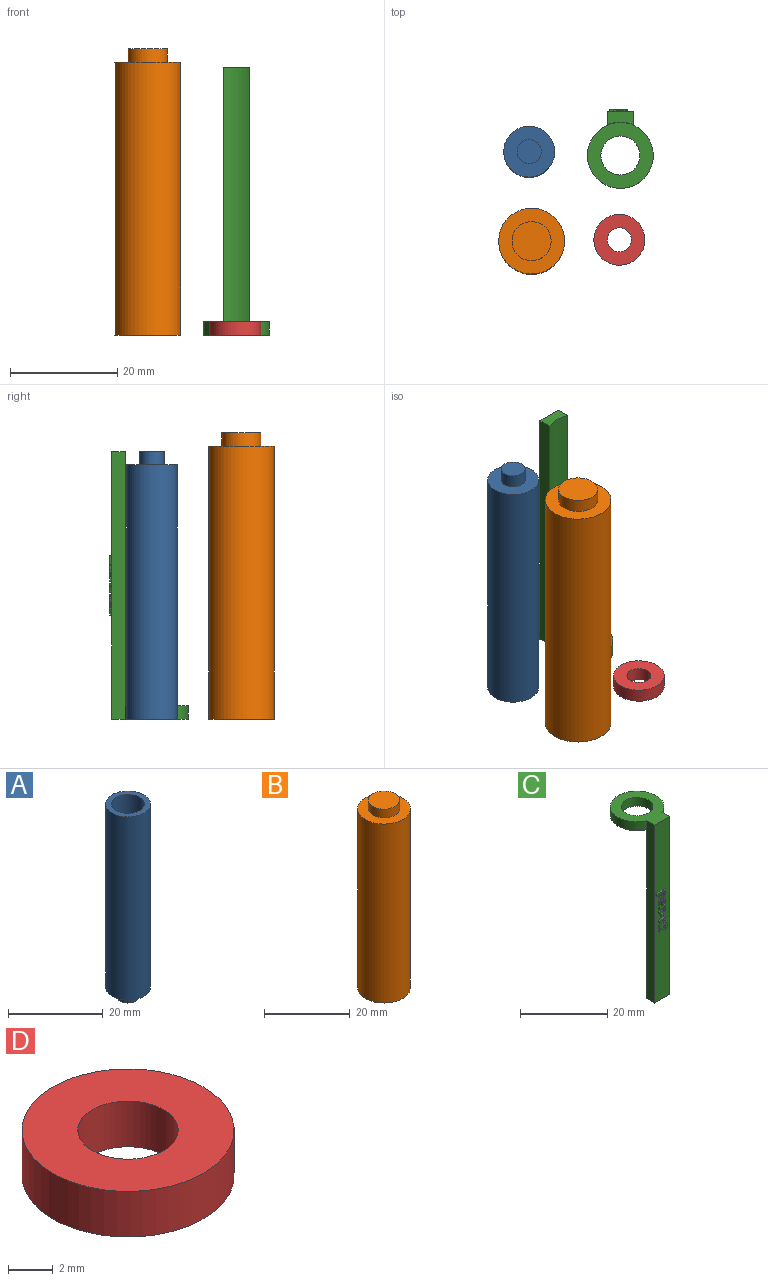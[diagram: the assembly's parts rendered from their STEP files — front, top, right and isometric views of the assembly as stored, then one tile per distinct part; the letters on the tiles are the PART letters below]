
ASSEMBLY  parts=4 mates=3
PART A: 7 faces, bbox 9.5x9.5x50 mm
  f0: cylinder r=3.5mm len=45mm, axis (0,0,-1), area 989.6mm2, adj f2,f3
  f1: cylinder r=4.75mm len=47.5mm, axis (0,0,-1), area 1417.6mm2, adj f2,f4
  f2: plane 9.5x9.5mm, normal (0,0,1), area 32.4mm2, adj f0,f1
  f3: plane 7x7mm, normal (0,0,1), area 38.5mm2, adj f0
  f4: plane 9.5x9.5mm, normal (0,0,-1), area 55mm2, adj f1,f5
  f5: cylinder r=2.25mm len=4.5mm, axis (0,0,1), area 35.3mm2, adj f4,f6
  f6: plane 4.5x4.5mm, normal (0,0,-1), area 15.9mm2, adj f5
PART B: 7 faces, bbox 12.3x12.3x53.5 mm
  f0: cylinder r=4.9mm len=50mm, axis (0,0,-1), area 1539.4mm2, adj f2,f3
  f1: cylinder r=6.15mm len=51mm, axis (0,0,-1), area 1970.7mm2, adj f2,f4
  f2: plane 12.3x12.3mm, normal (0,0,-1), area 43.4mm2, adj f0,f1
  f3: plane 9.8x9.8mm, normal (0,0,-1), area 75.4mm2, adj f0
  f4: plane 12.3x12.3mm, normal (0,0,1), area 77mm2, adj f1,f5
  f5: cylinder r=3.65mm len=7.3mm, axis (0,0,-1), area 57.3mm2, adj f4,f6
  f6: plane 7.3x7.3mm, normal (0,0,1), area 41.9mm2, adj f5
PART C: 115 faces, bbox 12.3x14.7x50 mm
  f0: plane 50x4.89mm, normal (0,-1,0), area 231.9mm2, adj f2,f6,f7,f8,f16,f17,f18,f19
  f1: cylinder r=6.15mm len=12.3mm, axis (0,0,-1), area 84mm2, adj f2,f4,f6,f7
  f2: plane 14.29x12.3mm, normal (0,0,1), area 87.5mm2, adj f0,f1,f3,f6,f7
  f3: cylinder r=3.65mm len=7.3mm, axis (0,0,-1), area 57.3mm2, adj f2,f4
  f4: plane 12.3x12.3mm, normal (0,0,-1), area 77mm2, adj f1,f3,f5
  f5: cylinder r=6.15mm len=47.5mm, axis (0,0,1), area 238.7mm2, adj f4,f6,f7,f8
  f6: plane 50x2.5mm, normal (-1,0,0), area 125mm2, adj f0,f1,f2,f5,f8
  f7: plane 50x2.5mm, normal (1,0,0), area 125mm2, adj f0,f1,f2,f5,f8
  f8: plane 4.89x2.5mm, normal (0,0,-1), area 10.6mm2, adj f0,f5,f6,f7
  f9: extruded ~0.4x0.28mm, area 0.1mm2, adj f10,f31,f32,f33
  f10: extruded ~0.4x0.27mm, area 0.1mm2, adj f9,f11,f32,f33
  f11: extruded ~0.42x0.4mm, area 0.2mm2, adj f10,f12,f32,f33
  f12: extruded ~0.57x0.4mm, area 0.3mm2, adj f11,f13,f32,f33
  f13: extruded ~0.4x0.29mm, area 0.1mm2, adj f12,f14,f32,f33
  f14: extruded ~0.44x0.4mm, area 0.2mm2, adj f13,f15,f32,f33
  f15: plane 0.4x0.06mm, normal (0,0,-1), area 0mm2, adj f14,f31,f32,f33
  f16: extruded ~0.52x0.4mm, area 0.2mm2, adj f0,f17,f30,f32
  f17: extruded ~0.4x0.38mm, area 0.2mm2, adj f0,f16,f18,f32
  f18: extruded ~0.4x0.34mm, area 0.2mm2, adj f0,f17,f19,f32
  f19: extruded ~0.52x0.4mm, area 0.2mm2, adj f0,f18,f20,f32
  f20: extruded ~0.72x0.4mm, area 0.3mm2, adj f0,f19,f21,f32
  f21: extruded ~0.52x0.4mm, area 0.2mm2, adj f0,f20,f22,f32
  f22: extruded ~0.54x0.4mm, area 0.3mm2, adj f0,f21,f23,f32
  f23: plane 0.4x0.02mm, normal (1,0,0), area 0mm2, adj f0,f22,f24,f32
  f24: plane 0.4x0.24mm, normal (0.28,0,-0.96), area 0.1mm2, adj f0,f23,f25,f32
  f25: plane 0.42x0.4mm, normal (1,0,0), area 0.2mm2, adj f0,f24,f26,f32
  f26: plane 2.72x0.4mm, normal (0,0,1), area 1.1mm2, adj f0,f25,f27,f32
  f27: plane 0.51x0.4mm, normal (-1,0,0), area 0.2mm2, adj f0,f26,f28,f32
  f28: plane 0.76x0.4mm, normal (0,0,-1), area 0.3mm2, adj f0,f27,f29,f32
  f29: extruded ~0.4x0.27mm, area 0.1mm2, adj f0,f28,f30,f32
  f30: plane 0.4x0.03mm, normal (-1,0,0), area 0mm2, adj f0,f16,f29,f32
  f31: extruded ~0.4x0.39mm, area 0.2mm2, adj f9,f15,f32,f33
  f32: plane 2.75x1.76mm, normal (0,-1,0), area 2.8mm2, adj f9,f10,f11,f12,f13,f14,f15,f16
  f33: plane 1.13x0.72mm, normal (0,-1,0), area 0.7mm2, adj f9,f10,f11,f12,f13,f14,f15,f31
  f34: extruded ~0.71x0.4mm, area 0.3mm2, adj f0,f35,f53,f54
  f35: extruded ~0.4x0.37mm, area 0.2mm2, adj f0,f34,f36,f54
  f36: extruded ~0.4x0.29mm, area 0.1mm2, adj f0,f35,f37,f54
  f37: plane 0.4x0.4mm, normal (0,0,-1), area 0.2mm2, adj f0,f36,f38,f54
  f38: extruded ~0.4x0.32mm, area 0.1mm2, adj f0,f37,f39,f54
  f39: extruded ~0.4x0.32mm, area 0.1mm2, adj f0,f38,f40,f54
  f40: extruded ~0.4x0.34mm, area 0.1mm2, adj f0,f39,f41,f54
  f41: extruded ~0.4x0.34mm, area 0.1mm2, adj f0,f40,f42,f54
  f42: plane 1.22x0.4mm, normal (-1,0,0), area 0.5mm2, adj f0,f41,f43,f54
  f43: plane 0.4x0.25mm, normal (0,0,-1), area 0.1mm2, adj f0,f42,f44,f54
  f44: extruded ~0.63x0.4mm, area 0.3mm2, adj f0,f43,f45,f54
  f45: extruded ~0.62x0.4mm, area 0.3mm2, adj f0,f44,f46,f54
  f46: extruded ~0.66x0.4mm, area 0.3mm2, adj f0,f45,f47,f54
  f47: extruded ~0.73x0.4mm, area 0.3mm2, adj f0,f46,f53,f54
  f48: extruded ~0.4x0.26mm, area 0.1mm2, adj f49,f52,f54,f55
  f49: extruded ~0.4x0.26mm, area 0.1mm2, adj f48,f50,f54,f55
  f50: extruded ~0.4x0.29mm, area 0.1mm2, adj f49,f51,f54,f55
  f51: plane 0.72x0.4mm, normal (1,0,0), area 0.3mm2, adj f50,f52,f54,f55
  f52: extruded ~0.4x0.29mm, area 0.1mm2, adj f48,f51,f54,f55
  f53: extruded ~0.71x0.4mm, area 0.3mm2, adj f0,f34,f47,f54
  f54: plane 1.95x1.74mm, normal (0,-1,0), area 2.1mm2, adj f34,f35,f36,f37,f38,f39,f40,f41
  f55: plane 0.72x0.4mm, normal (0,-1,0), area 0.2mm2, adj f48,f49,f50,f51,f52
  f56: plane 0.51x0.4mm, normal (-1,0,0), area 0.2mm2, adj f0,f57,f72,f73
  f57: plane 1.23x0.4mm, normal (0,0,-1), area 0.5mm2, adj f0,f56,f58,f73
  f58: extruded ~0.51x0.4mm, area 0.2mm2, adj f0,f57,f59,f73
  f59: extruded ~0.5x0.4mm, area 0.2mm2, adj f0,f58,f60,f73
  f60: extruded ~0.4x0.34mm, area 0.1mm2, adj f0,f59,f61,f73
  f61: extruded ~0.4x0.24mm, area 0.1mm2, adj f0,f60,f62,f73
  f62: plane 0.4x0.03mm, normal (1,0,0), area 0mm2, adj f0,f61,f63,f73
  f63: plane 0.4x0.24mm, normal (0.28,0,-0.96), area 0.1mm2, adj f0,f62,f64,f73
  f64: plane 0.4x0.39mm, normal (1,0,0), area 0.2mm2, adj f0,f63,f65,f73
  f65: plane 1.89x0.4mm, normal (0,0,1), area 0.8mm2, adj f0,f64,f66,f73
  f66: plane 0.51x0.4mm, normal (-1,0,0), area 0.2mm2, adj f0,f65,f67,f73
  f67: plane 0.89x0.4mm, normal (0,0,-1), area 0.4mm2, adj f0,f66,f68,f73
  f68: extruded ~0.48x0.4mm, area 0.2mm2, adj f0,f67,f69,f73
  f69: extruded ~0.4x0.31mm, area 0.1mm2, adj f0,f68,f70,f73
  f70: extruded ~0.4x0.23mm, area 0.1mm2, adj f0,f69,f71,f73
  f71: extruded ~0.4x0.31mm, area 0.1mm2, adj f0,f70,f72,f73
  f72: plane 1.1x0.4mm, normal (0,0,1), area 0.4mm2, adj f0,f56,f71,f73
  f73: plane 1.92x1.74mm, normal (0,-1,0), area 2.2mm2, adj f56,f57,f58,f59,f60,f61,f62,f63
  f74: plane 0.42x0.4mm, normal (0,0,1), area 0.2mm2, adj f0,f75,f77,f78
  f75: plane 0.91x0.4mm, normal (-1,0,0), area 0.4mm2, adj f0,f74,f76,f78
  f76: plane 0.42x0.4mm, normal (0,0,-1), area 0.2mm2, adj f0,f75,f77,f78
  f77: plane 0.91x0.4mm, normal (1,0,0), area 0.4mm2, adj f0,f74,f76,f78
  f78: plane 0.91x0.42mm, normal (0,-1,0), area 0.4mm2, adj f74,f75,f76,f77
  f79: plane 1.89x0.72mm, normal (-0.36,0,0.93), area 0.8mm2, adj f0,f80,f88,f89
  f80: plane 0.53x0.4mm, normal (-1,0,0), area 0.2mm2, adj f0,f79,f81,f89
  f81: plane 1.89x0.72mm, normal (-0.36,0,-0.93), area 0.8mm2, adj f0,f80,f82,f89
  f82: plane 0.54x0.4mm, normal (1,0,0), area 0.2mm2, adj f0,f81,f83,f89
  f83: plane 1.07x0.4mm, normal (0.32,0,0.95), area 0.5mm2, adj f0,f82,f84,f89
  f84: extruded ~0.4x0.39mm, area 0.2mm2, adj f0,f83,f85,f89
  f85: plane 0.4x0.01mm, normal (1,0,0), area 0mm2, adj f0,f84,f86,f89
  f86: extruded ~0.4x0.39mm, area 0.2mm2, adj f0,f85,f87,f89
  f87: plane 1.07x0.4mm, normal (0.32,0,-0.95), area 0.5mm2, adj f0,f86,f88,f89
  f88: plane 0.54x0.4mm, normal (1,0,0), area 0.2mm2, adj f0,f79,f87,f89
  f89: plane 1.97x1.89mm, normal (0,-1,0), area 1.8mm2, adj f79,f80,f81,f82,f83,f84,f85,f86
  f90: plane 1.72x0.4mm, normal (-1,0,0), area 0.7mm2, adj f0,f91,f113,f114
  f91: plane 0.44x0.4mm, normal (0,0,-1), area 0.2mm2, adj f0,f90,f92,f114
  f92: plane 1.07x0.4mm, normal (1,0,0), area 0.4mm2, adj f0,f91,f93,f114
  f93: plane 0.4x0.02mm, normal (0,0,-1), area 0mm2, adj f0,f92,f94,f114
  f94: plane 0.4x0.32mm, normal (-0.73,0,-0.69), area 0.2mm2, adj f0,f93,f95,f114
  f95: extruded ~0.45x0.44mm, area 0.3mm2, adj f0,f94,f96,f114
  f96: extruded ~0.4x0.31mm, area 0.1mm2, adj f0,f95,f97,f114
  f97: extruded ~0.4x0.32mm, area 0.1mm2, adj f0,f96,f98,f114
  f98: extruded ~0.4x0.35mm, area 0.1mm2, adj f0,f97,f99,f114
  f99: extruded ~0.4x0.28mm, area 0.1mm2, adj f0,f98,f100,f114
  f100: extruded ~0.41x0.4mm, area 0.2mm2, adj f0,f99,f101,f114
  f101: extruded ~0.4x0.32mm, area 0.1mm2, adj f0,f100,f102,f114
  f102: extruded ~0.4x0.26mm, area 0.1mm2, adj f0,f101,f103,f114
  f103: extruded ~0.4x0.3mm, area 0.1mm2, adj f0,f102,f104,f114
  f104: plane 0.4x0.34mm, normal (-0.65,0,0.76), area 0.2mm2, adj f0,f103,f105,f114
  f105: extruded ~0.4x0.28mm, area 0.1mm2, adj f0,f104,f106,f114
  f106: extruded ~0.4x0.28mm, area 0.1mm2, adj f0,f105,f107,f114
  f107: extruded ~0.4x0.22mm, area 0.1mm2, adj f0,f106,f108,f114
  f108: extruded ~0.4x0.22mm, area 0.1mm2, adj f0,f107,f109,f114
  f109: extruded ~0.4x0.19mm, area 0.1mm2, adj f0,f108,f110,f114
  f110: extruded ~0.4x0.2mm, area 0.1mm2, adj f0,f109,f111,f114
  f111: extruded ~0.4x0.39mm, area 0.2mm2, adj f0,f110,f112,f114
  f112: plane 0.63x0.62mm, normal (0.7,0,0.71), area 0.4mm2, adj f0,f111,f113,f114
  f113: plane 0.4x0.36mm, normal (0,0,1), area 0.1mm2, adj f0,f90,f112,f114
  f114: plane 2.5x1.73mm, normal (0,-1,0), area 2.3mm2, adj f90,f91,f92,f93,f94,f95,f96,f97
PART D: 4 faces, bbox 9.5x9.5x2.5 mm
  f0: cylinder r=2.25mm len=4.5mm, axis (0,0,1), area 35.3mm2, adj f2,f3
  f1: cylinder r=4.75mm len=9.5mm, axis (0,0,1), area 74.6mm2, adj f2,f3
  f2: plane 9.5x9.5mm, normal (0,0,-1), area 55mm2, adj f0,f1
  f3: plane 9.5x9.5mm, normal (0,0,1), area 55mm2, adj f0,f1
PLACE A rot(axis=(1,0,0),180deg) t=(-8.49,8.17,-9.24)mm
PLACE B t=(-8.04,-8.55,-99.24)mm
PLACE C rot(axis=(1,0,0),180deg) t=(8.54,7.53,44.26)mm
PLACE D t=(8.35,-8.22,-49.24)mm
MATE planar B.f1 <-> A.f0  axis (0,0,-1) through (-8.04,-8.55,-54.24)mm
MATE planar C.f3 <-> D.f1  axis (0,0,-1) through (8.54,7.53,-54.24)mm
MATE planar D.f1 <-> A.f0  axis (0,0,-1) through (8.35,-8.22,-54.24)mm
